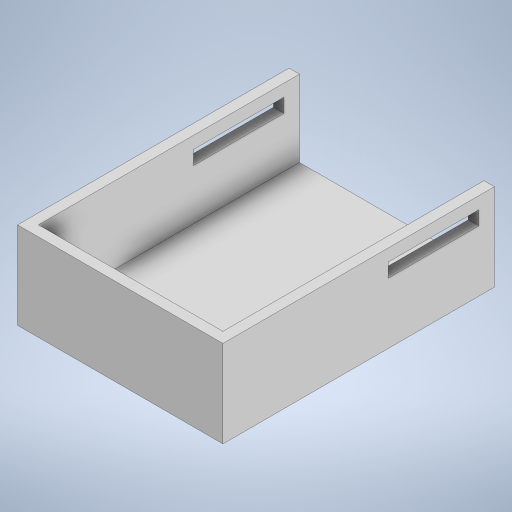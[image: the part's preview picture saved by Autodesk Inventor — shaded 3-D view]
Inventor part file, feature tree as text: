
AUTODESK INVENTOR PART (.ipt)
format: ipt  version: 2023 (Build 270158000, 158)  size: 237,568 bytes
history: native  units: in
note: dims shown in document units (in); Inventor stores cm internally (conversion verified against a paired STEP export)
features: sketch x4, extrude x3, shell x1
ambient origin geometry x8: Origin, YZ Plane, XZ Plane, XY Plane, X Axis, Y Axis, Z Axis, Center Point
bodies: Solid1 (feature_tree)
feature tree (8):
  extrude  "Extrusion1"  Depth=3.0709in
  shell  "Shell1"  Thickness=0.9843in
  sketch  "Sketch4"  dims[d4=0.1181in d17=0.3937in d18=0.0in]
  extrude  "Extrusion3"  Depth=0.1181in TaperAngle=0.0deg
  extrude  "Extrusion4"  Depth=0.1575in
  sketch  "Sketch2"  dims[d0=2.3228in d1=3.0709in d2=0.9843in d3=0.0in]
  sketch  "Sketch5"  dims[d19=1.0236in d20=0.1575in]
  sketch  "Sketch6"  dims[d21=0.1772in d22=0.689in d23=0.0in d24=0.0in d13=0.0197in d14=0.0344in d15=0.0197in d16=0.0344in]
